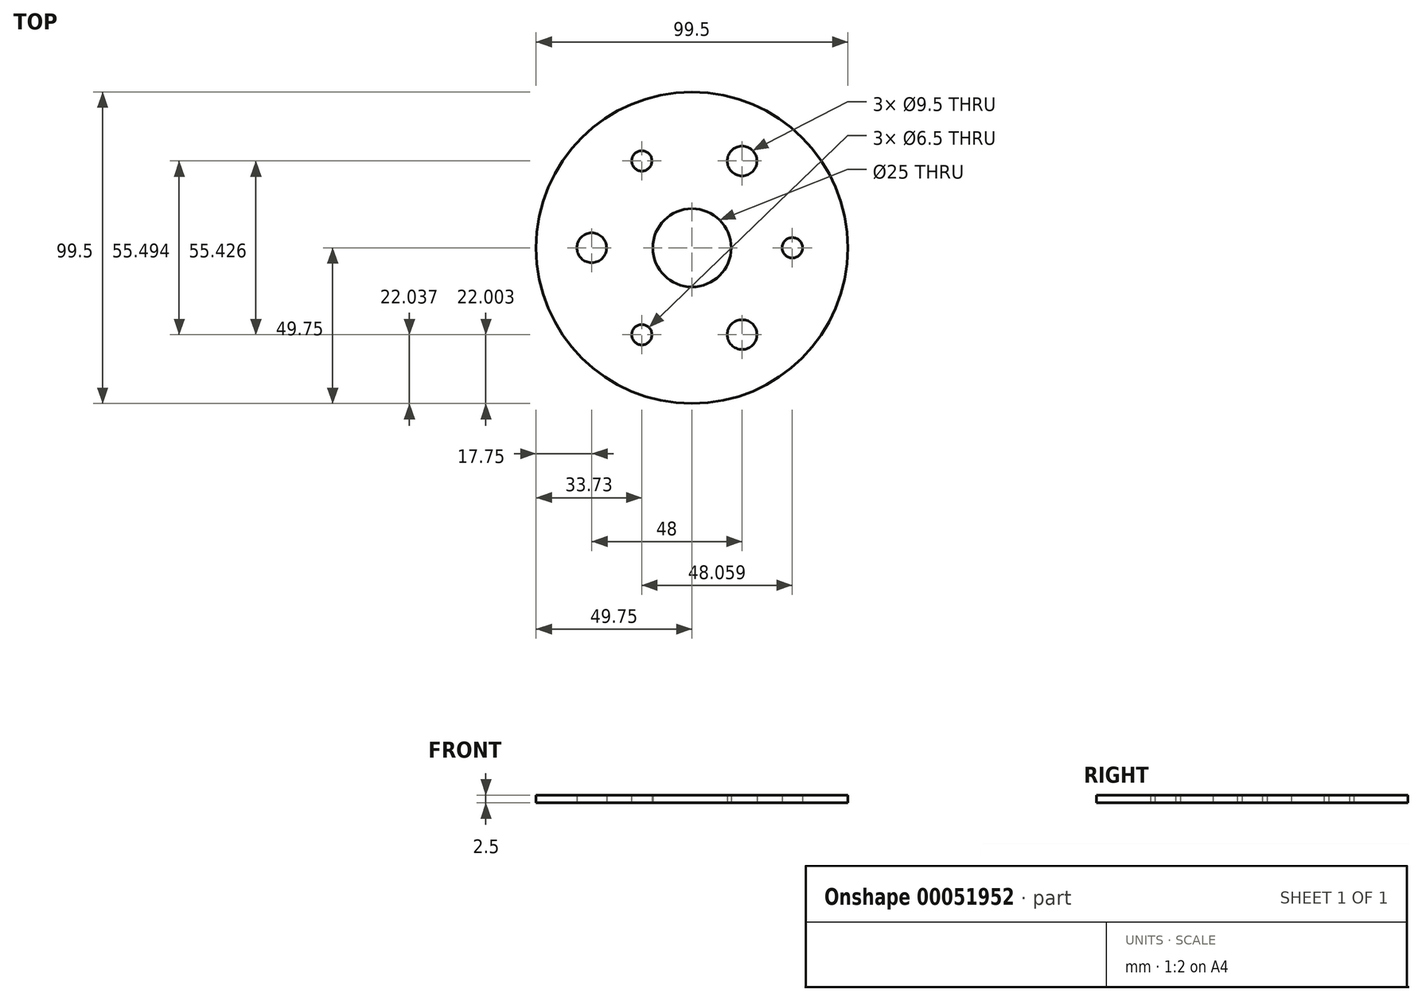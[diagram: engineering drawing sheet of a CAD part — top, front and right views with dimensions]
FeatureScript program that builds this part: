
annotation { "Feature Type Name" : "Feature", "Feature Type Description" : "" }
export const myFeature = defineFeature(function(context is Context, id is Id, definition is map)
    precondition{}
    {
        {
            var Q0;
            Q0=qCreatedBy(makeId("Top.planeOp"),FACE);
            var sketch = newSketch(context, id + "F0", { "sketchPlane" : qUnion([Q0])});
            skCircle(sketch, "E0", {"center": v(0, 0) * mm, "radius": 49.75 * mm});
            skCircle(sketch, "E1", {"center": v(0, 0) * mm, "radius": 12.5 * mm});
            skCircle(sketch, "E2", {"center": v(-32, 0) * mm, "radius": 4.75 * mm});
            skCircle(sketch, "E3.1.0", {"center": v(16, -27.71) * mm, "radius": 4.75 * mm});
            skCircle(sketch, "E3.2.0", {"center": v(16, 27.71) * mm, "radius": 4.75 * mm});
            skCircle(sketch, "E4", {"center": v(32.04, 0) * mm, "radius": 3.25 * mm});
            skCircle(sketch, "E5.1.0", {"center": v(-16.02, 27.75) * mm, "radius": 3.25 * mm});
            skCircle(sketch, "E5.2.0", {"center": v(-16.02, -27.75) * mm, "radius": 3.25 * mm});
            skSolve(sketch);
        }
        {
            var Q0;
            Q0 = qSketchRegion(id + "F0", true);
            extrude(context, id + "F1", {"entities" : qUnion([Q0]), "depth" : 2.5 * mm});
        }
    });
